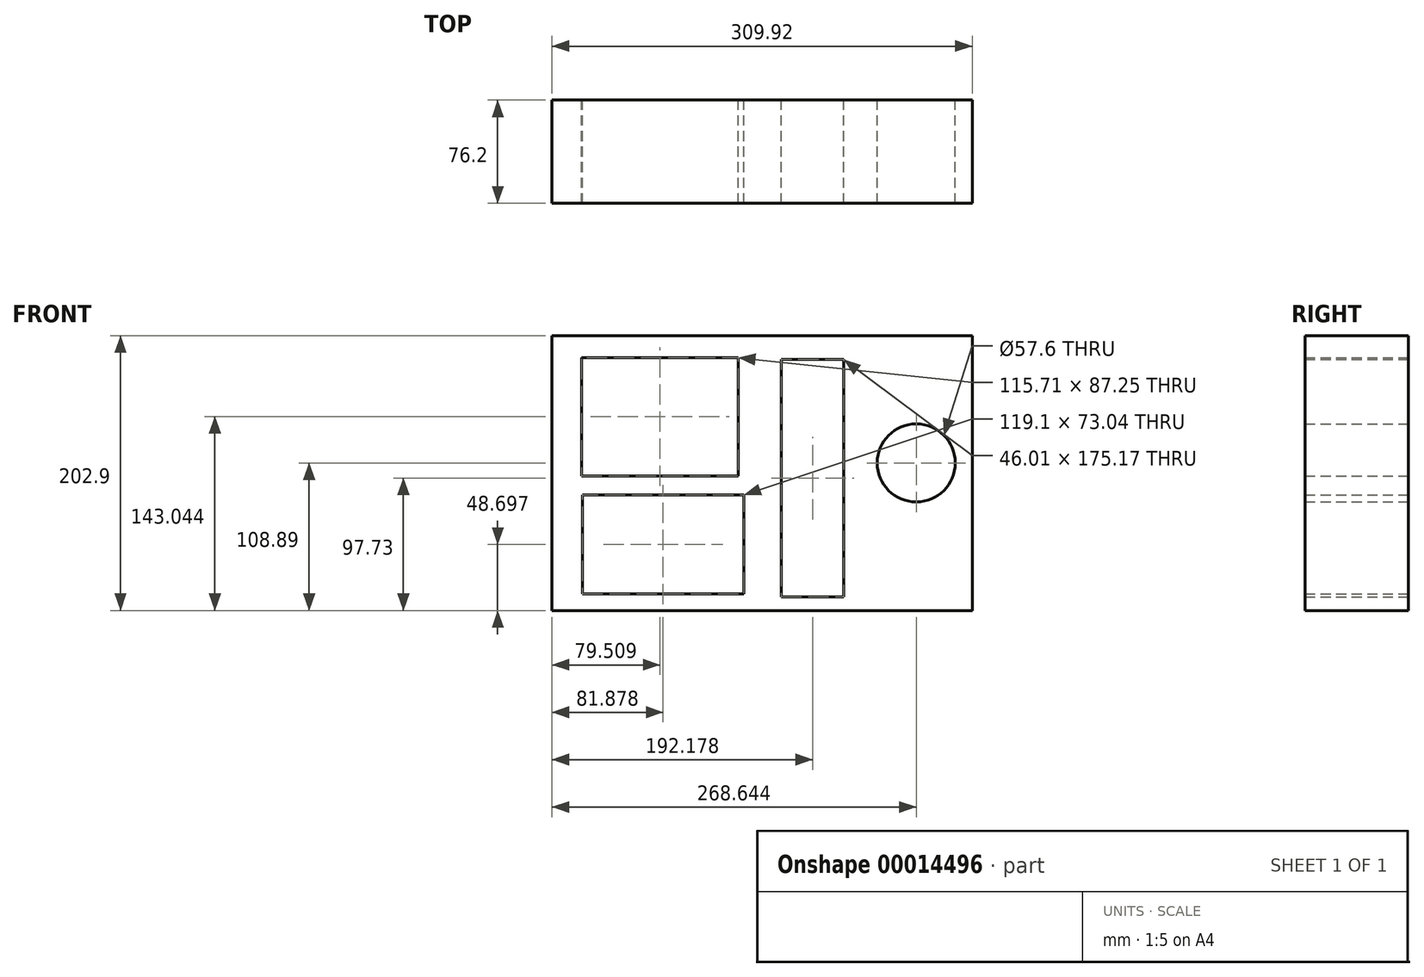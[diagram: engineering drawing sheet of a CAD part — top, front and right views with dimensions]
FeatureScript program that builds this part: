
annotation { "Feature Type Name" : "Feature", "Feature Type Description" : "" }
export const myFeature = defineFeature(function(context is Context, id is Id, definition is map)
    precondition{}
    {
        {
            var Q0;
            Q0=qCreatedBy(makeId("Front.planeOp"),FACE);
            var sketch = newSketch(context, id + "F0", { "sketchPlane" : qUnion([Q0])});
            skLineSegment(sketch, "E0", {"start": v(-154.96, -101.45) * mm, "end": v(154.96, -101.45) * mm});
            skLineSegment(sketch, "E1", {"start": v(154.96, -101.45) * mm, "end": v(154.96, 101.45) * mm});
            skLineSegment(sketch, "E2", {"start": v(154.96, 101.45) * mm, "end": v(-154.96, 101.45) * mm});
            skLineSegment(sketch, "E3", {"start": v(-154.96, 101.45) * mm, "end": v(-154.96, -101.45) * mm});
            skLineSegment(sketch, "E4", {"start": v(-133.3, 85.22) * mm, "end": v(-17.6, 85.22) * mm});
            skLineSegment(sketch, "E5", {"start": v(-17.6, 85.22) * mm, "end": v(-17.6, -2.03) * mm});
            skLineSegment(sketch, "E6", {"start": v(-17.6, -2.03) * mm, "end": v(-133.3, -2.03) * mm});
            skLineSegment(sketch, "E7", {"start": v(-133.3, -2.03) * mm, "end": v(-133.3, 85.22) * mm});
            skLineSegment(sketch, "E8", {"start": v(-132.63, -16.23) * mm, "end": v(-13.53, -16.23) * mm});
            skLineSegment(sketch, "E9", {"start": v(-13.53, -16.23) * mm, "end": v(-13.53, -89.27) * mm});
            skLineSegment(sketch, "E10", {"start": v(-13.53, -89.27) * mm, "end": v(-132.63, -89.27) * mm});
            skLineSegment(sketch, "E11", {"start": v(-132.63, -89.27) * mm, "end": v(-132.63, -16.23) * mm});
            skLineSegment(sketch, "E12", {"start": v(14.21, 83.86) * mm, "end": v(60.23, 83.86) * mm});
            skLineSegment(sketch, "E13", {"start": v(60.23, 83.86) * mm, "end": v(60.23, -91.3) * mm});
            skLineSegment(sketch, "E14", {"start": v(60.23, -91.3) * mm, "end": v(14.21, -91.3) * mm});
            skLineSegment(sketch, "E15", {"start": v(14.21, -91.3) * mm, "end": v(14.21, 83.86) * mm});
            skCircle(sketch, "E16", {"center": v(113.68, 7.44) * mm, "radius": 28.8 * mm});
            skSolve(sketch);
        }
        {
            var Q0;
            Q0=makeQuery(id+"F0.imprint","IMPRINT",FACE,{"disambiguationData":[TD([[makeQuery(id+"F0.imprint","IMPRINT",EDGE,{"derivedFrom":sQuery(id+"F0.wireOp",EDGE,"E0")}),1.0]])]});
            extrude(context, id + "F1", {"entities" : qUnion([Q0]), "depth" : 76.2 * mm});
        }
    });
